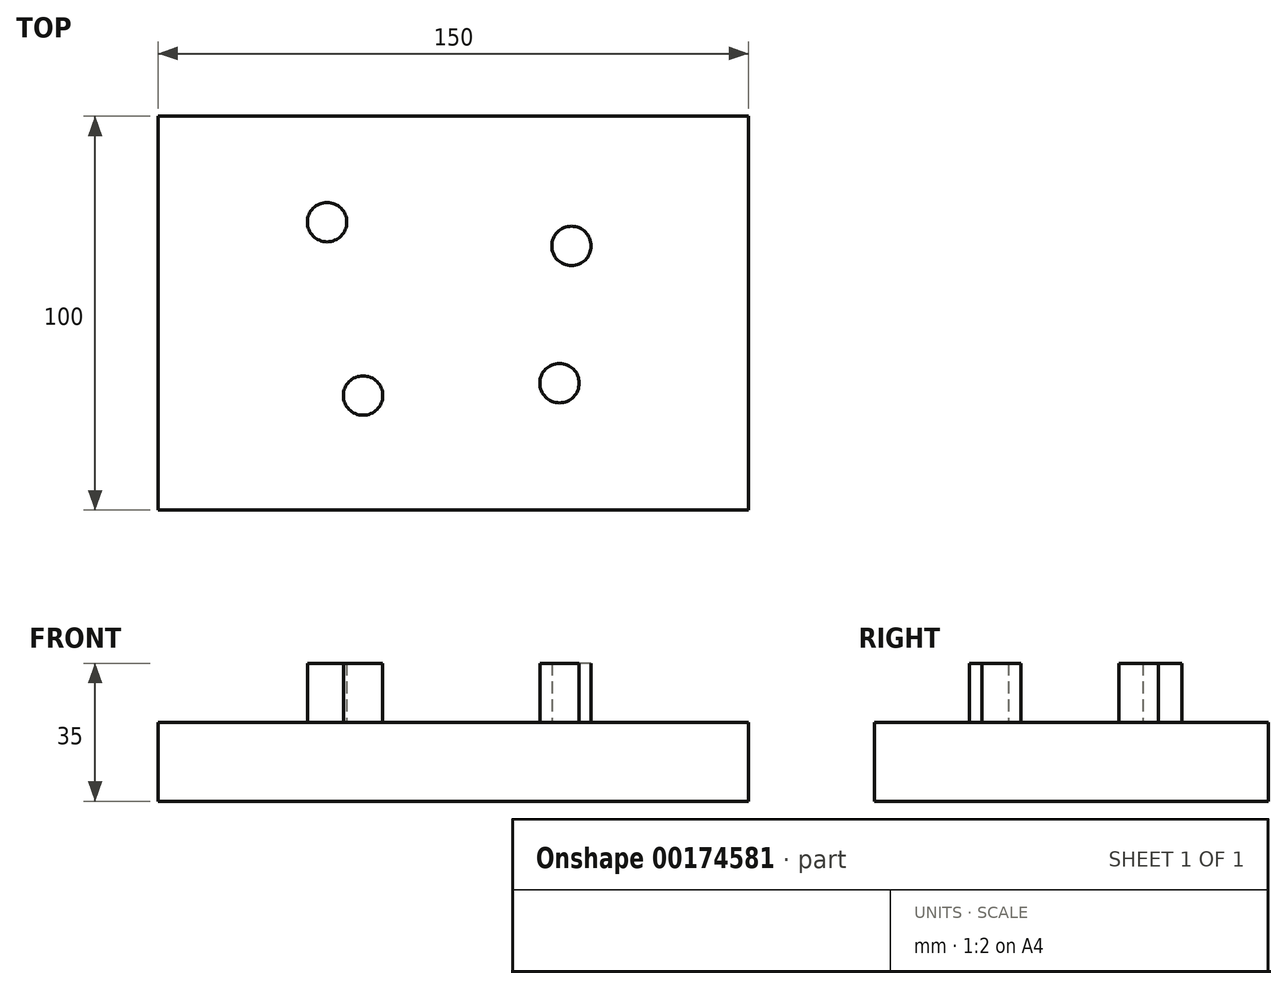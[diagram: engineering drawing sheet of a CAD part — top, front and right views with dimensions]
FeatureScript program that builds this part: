
annotation { "Feature Type Name" : "Feature", "Feature Type Description" : "" }
export const myFeature = defineFeature(function(context is Context, id is Id, definition is map)
    precondition{}
    {
        {
            var Q0;
            Q0=qCreatedBy(makeId("Top.planeOp"),FACE);
            var sketch = newSketch(context, id + "F0", { "sketchPlane" : qUnion([Q0])});
            skLineSegment(sketch, "E0.bottom", {"start": v(75, 50) * mm, "end": v(-75, 50) * mm});
            skLineSegment(sketch, "E0.top", {"start": v(75, -50) * mm, "end": v(-75, -50) * mm});
            skLineSegment(sketch, "E0.left", {"start": v(75, 50) * mm, "end": v(75, -50) * mm});
            skLineSegment(sketch, "E0.right", {"start": v(-75, 50) * mm, "end": v(-75, -50) * mm});
            skPoint(sketch, "E0.middle", {"position": v(0, 0) * mm});
            skSolve(sketch);
        }
        {
            var Q0;
            Q0=makeQuery(id+"F0.imprint","IMPRINT",FACE,{"disambiguationData":[TD([[makeQuery(id+"F0.imprint","IMPRINT",EDGE,{"derivedFrom":sQuery(id+"F0.wireOp",EDGE,"E0.bottom")}),1.0]])]});
            extrude(context, id + "F1", {"entities" : qUnion([Q0]), "depth" : 20 * mm});
        }
        {
            var Q0;
            Q0=makeQuery(id+"F1.opExtrude","CAP_FACE",FACE,{"disambiguationData":[OSD([sQuery(id+"F0.wireOp",EDGE,"E0.bottom"),sQuery(id+"F0.wireOp",EDGE,"E0.top"),sQuery(id+"F0.wireOp",EDGE,"E0.left"),sQuery(id+"F0.wireOp",EDGE,"E0.right")])],"isStart":false});
            var sketch = newSketch(context, id + "F2", { "sketchPlane" : qUnion([Q0])});
            skCircle(sketch, "E1", {"center": v(-32.1, 23.12) * mm, "radius": 5 * mm});
            skCircle(sketch, "E2", {"center": v(-22.95, -20.94) * mm, "radius": 5 * mm});
            skCircle(sketch, "E3", {"center": v(30, 17.08) * mm, "radius": 5 * mm});
            skCircle(sketch, "E4", {"center": v(26.95, -17.79) * mm, "radius": 5 * mm});
            skSolve(sketch);
        }
        {
            var Q0;
            Q0=makeQuery(id+"F2.imprint","IMPRINT",FACE,{"disambiguationData":[TD([[makeQuery(id+"F2.imprint","IMPRINT",EDGE,{"derivedFrom":sQuery(id+"F2.wireOp",EDGE,"E4")}),1.0]])]});
            var Q1;
            Q1=makeQuery(id+"F2.imprint","IMPRINT",FACE,{"disambiguationData":[TD([[makeQuery(id+"F2.imprint","IMPRINT",EDGE,{"derivedFrom":sQuery(id+"F2.wireOp",EDGE,"E3")}),1.0]])]});
            var Q2;
            Q2=makeQuery(id+"F2.imprint","IMPRINT",FACE,{"disambiguationData":[TD([[makeQuery(id+"F2.imprint","IMPRINT",EDGE,{"derivedFrom":sQuery(id+"F2.wireOp",EDGE,"E1")}),1.0]])]});
            var Q3;
            Q3=makeQuery(id+"F2.imprint","IMPRINT",FACE,{"disambiguationData":[TD([[makeQuery(id+"F2.imprint","IMPRINT",EDGE,{"derivedFrom":sQuery(id+"F2.wireOp",EDGE,"E2")}),1.0]])]});
            extrude(context, id + "F3", {"entities" : qUnion([Q0, Q1, Q2, Q3]), "operationType" : NewBodyOperationType.ADD, "depth" : 15 * mm});
        }
    });
